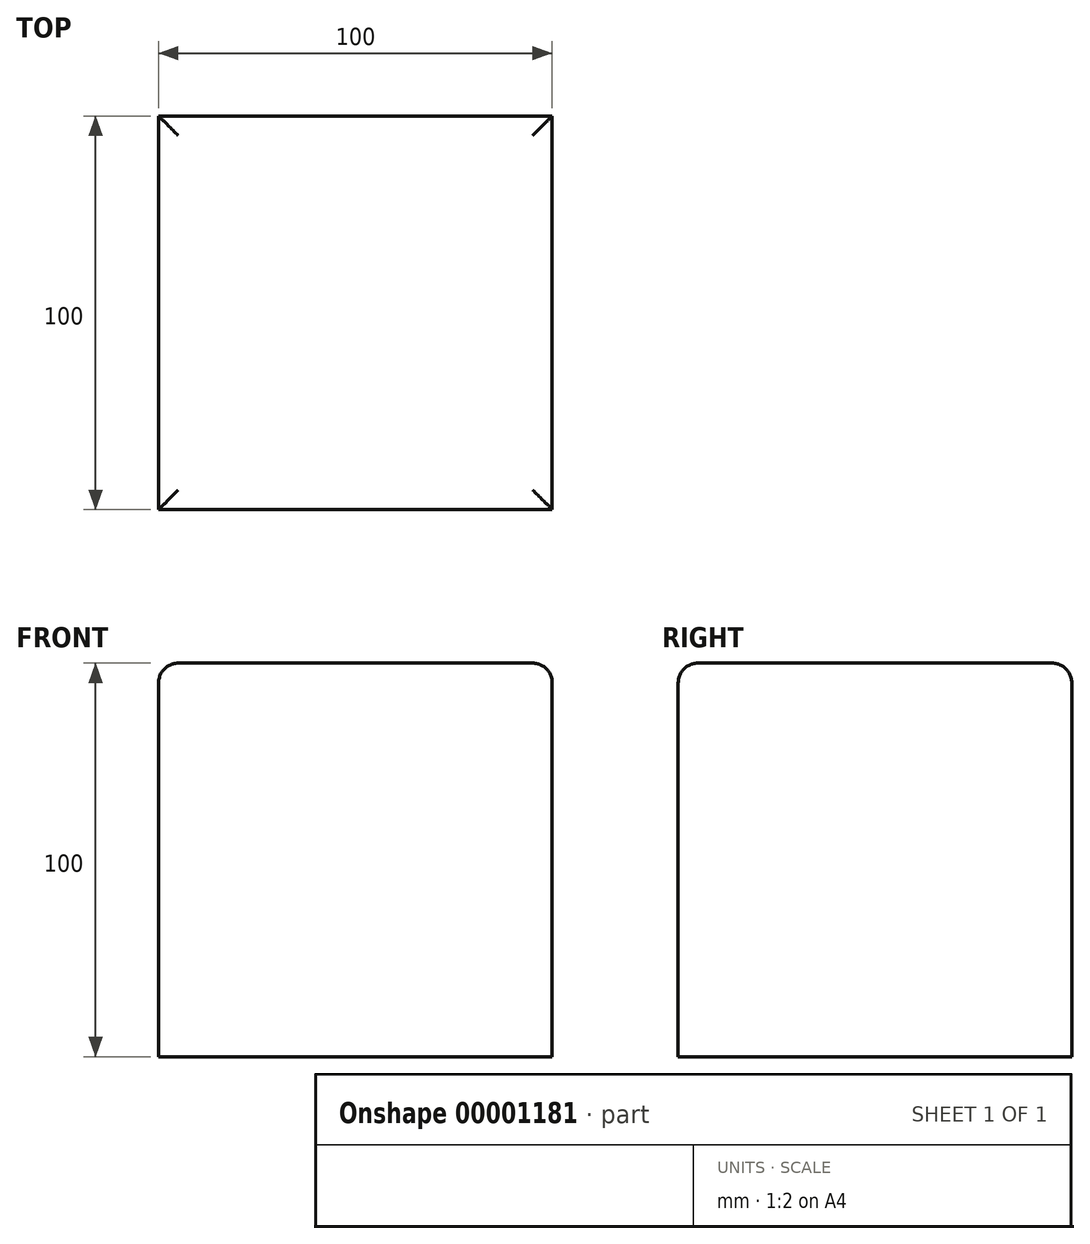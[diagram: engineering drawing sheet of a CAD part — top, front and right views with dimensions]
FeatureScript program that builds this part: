
annotation { "Feature Type Name" : "Feature", "Feature Type Description" : "" }
export const myFeature = defineFeature(function(context is Context, id is Id, definition is map)
    precondition{}
    {
        {
            var Q0;
            Q0=qCreatedBy(makeId("Front.planeOp"),FACE);
            var sketch = newSketch(context, id + "F0", { "sketchPlane" : qUnion([Q0])});
            skLineSegment(sketch, "E0.rect.bottom", {"start": v(50, 50) * mm, "end": v(-50, 50) * mm});
            skLineSegment(sketch, "E0.rect.top", {"start": v(50, -50) * mm, "end": v(-50, -50) * mm});
            skLineSegment(sketch, "E0.rect.left", {"start": v(50, 50) * mm, "end": v(50, -50) * mm});
            skLineSegment(sketch, "E0.rect.right", {"start": v(-50, 50) * mm, "end": v(-50, -50) * mm});
            skPoint(sketch, "E0.rect.middle", {"position": v(0, 0) * mm});
            skSolve(sketch);
        }
        {
            var Q0;
            Q0=makeQuery(id+"F0.imprint","IMPRINT",FACE,{"disambiguationData":[TD([[makeQuery(id+"F0.imprint","IMPRINT",EDGE,{"derivedFrom":sQuery(id+"F0.wireOp",EDGE,"E0.rect.bottom")}),1.0]])]});
            extrude(context, id + "F1", {"entities" : qUnion([Q0]), "endBound" : BoundingType.SYMMETRIC, "depth" : 100 * mm});
        }
        {
            var Q0;
            Q0=makeQuery(id+"F1.opExtrude","SWEPT_EDGE",EDGE,{"disambiguationData":[OSD([sQuery(id+"F0.wireOp",EDGE,"E0.rect.bottom"),sQuery(id+"F0.wireOp",EDGE,"E0.rect.left")])]});
            var Q1;
            Q1=makeQuery(id+"F1.opExtrude","CAP_EDGE",EDGE,{"disambiguationData":[OSD([sQuery(id+"F0.wireOp",EDGE,"E0.rect.bottom")])],"isStart":false});
            var Q2;
            Q2=makeQuery(id+"F1.opExtrude","CAP_EDGE",EDGE,{"disambiguationData":[OSD([sQuery(id+"F0.wireOp",EDGE,"E0.rect.bottom")])],"isStart":true});
            var Q3;
            Q3=makeQuery(id+"F1.opExtrude","SWEPT_EDGE",EDGE,{"disambiguationData":[OSD([sQuery(id+"F0.wireOp",EDGE,"E0.rect.bottom"),sQuery(id+"F0.wireOp",EDGE,"E0.rect.right")])]});
            fillet(context, id + "F2", {"entities" : qUnion([Q0, Q1, Q2, Q3]), "radius" : 5 * mm, "tangentPropagation" : true, "allowEdgeOverflow" : false});
        }
    });
